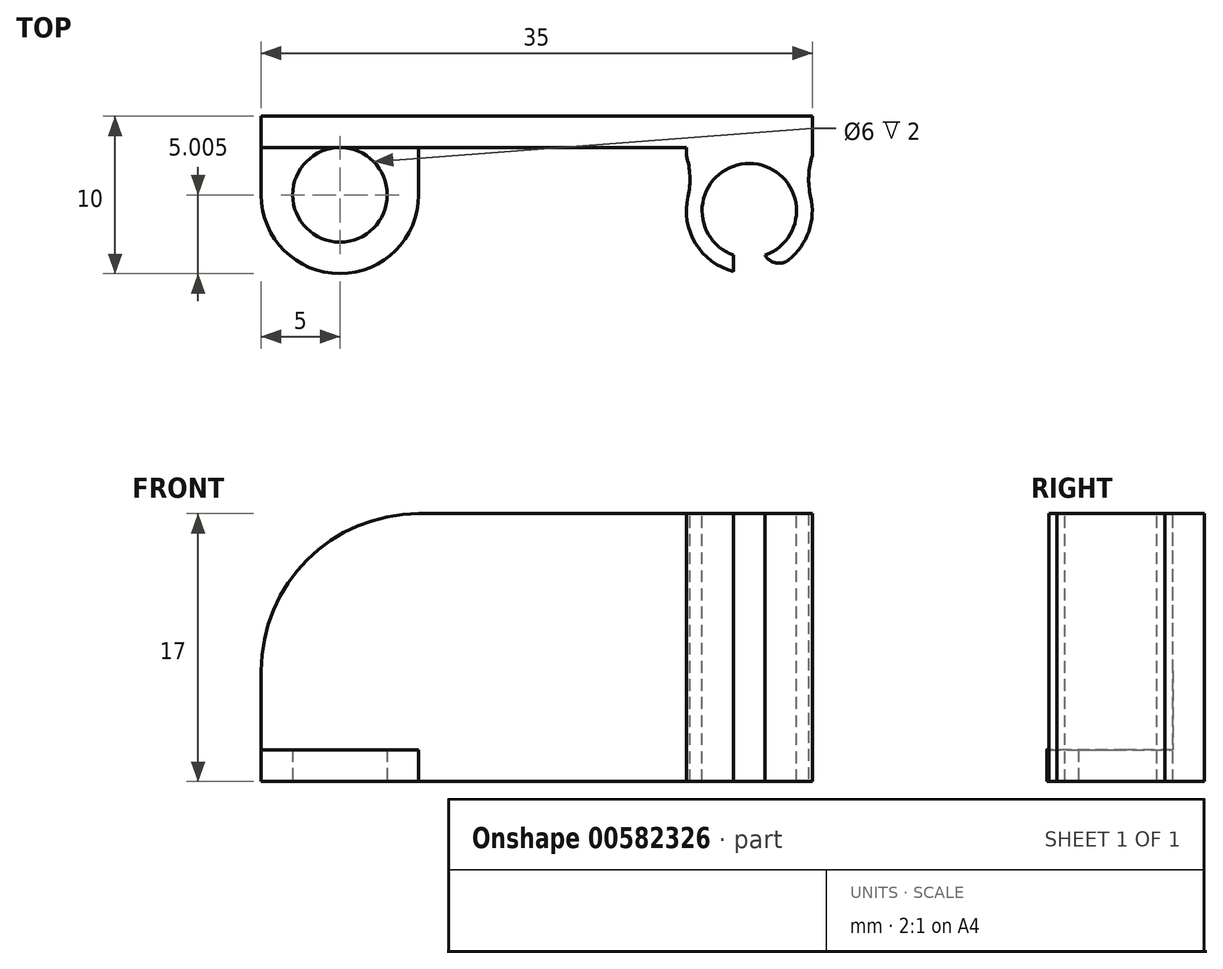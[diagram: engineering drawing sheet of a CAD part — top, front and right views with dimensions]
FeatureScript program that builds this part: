
annotation { "Feature Type Name" : "Feature", "Feature Type Description" : "" }
export const myFeature = defineFeature(function(context is Context, id is Id, definition is map)
    precondition{}
    {
        {
            var Q0;
            Q0=qCreatedBy(makeId("Top.planeOp"),FACE);
            var sketch = newSketch(context, id + "F0", { "sketchPlane" : qUnion([Q0])});
            skLineSegment(sketch, "E0.bottom", {"start": v(-13.22, 16.13) * mm, "end": v(-3.22, 16.13) * mm});
            skLineSegment(sketch, "E0.top", {"start": v(-13.22, 6.13) * mm, "end": v(-3.22, 6.13) * mm});
            skLineSegment(sketch, "E0.left", {"start": v(-13.22, 16.13) * mm, "end": v(-13.22, 6.13) * mm});
            skLineSegment(sketch, "E0.right", {"start": v(-3.22, 16.13) * mm, "end": v(-3.22, 6.13) * mm});
            skSolve(sketch);
        }
        {
            var Q0;
            Q0 = qSketchRegion(id + "F0", true);
            extrude(context, id + "F1", {"entities" : qUnion([Q0]), "depth" : 2 * mm, "offsetDistance" : 25 * mm});
        }
        {
            var Q0;
            Q0=makeQuery(id+"F1.opExtrude","CAP_FACE",FACE,{"disambiguationData":[OSD([sQuery(id+"F0.wireOp",EDGE,"E0.bottom"),sQuery(id+"F0.wireOp",EDGE,"E0.top"),sQuery(id+"F0.wireOp",EDGE,"E0.left"),sQuery(id+"F0.wireOp",EDGE,"E0.right")])],"isStart":false});
            var sketch = newSketch(context, id + "F2", { "sketchPlane" : qUnion([Q0])});
            skLineSegment(sketch, "E1.bottom", {"start": v(-13.22, 16.13) * mm, "end": v(-3.22, 16.13) * mm});
            skLineSegment(sketch, "E1.top", {"start": v(-13.22, 14.13) * mm, "end": v(-3.22, 14.13) * mm});
            skLineSegment(sketch, "E1.left", {"start": v(-13.22, 16.13) * mm, "end": v(-13.22, 14.13) * mm});
            skLineSegment(sketch, "E1.right", {"start": v(-3.22, 16.13) * mm, "end": v(-3.22, 14.13) * mm});
            skSolve(sketch);
        }
        {
            var Q0;
            Q0 = qSketchRegion(id + "F2", true);
            extrude(context, id + "F3", {"entities" : qUnion([Q0]), "operationType" : NewBodyOperationType.ADD, "depth" : 15 * mm, "offsetDistance" : 25 * mm});
        }
        {
            var Q0;
            Q0=makeQuery(id+"F3.boolean.opBoolean","MERGE",FACE,{"derivedFrom":[makeQuery(id+"F1.opExtrude","SWEPT_FACE",FACE,{"disambiguationData":[OSD([sQuery(id+"F0.wireOp",EDGE,"E0.right")])]}),makeQuery(id+"F3.opExtrude","SWEPT_FACE",FACE,{"disambiguationData":[OSD([sQuery(id+"F2.wireOp",EDGE,"E1.right")])]})]});
            var sketch = newSketch(context, id + "F4", { "sketchPlane" : qUnion([Q0])});
            skLineSegment(sketch, "E2.bottom", {"start": v(16.13, 0) * mm, "end": v(14.13, 0) * mm});
            skLineSegment(sketch, "E2.top", {"start": v(16.13, 17) * mm, "end": v(14.13, 17) * mm});
            skLineSegment(sketch, "E2.left", {"start": v(16.13, 0) * mm, "end": v(16.13, 17) * mm});
            skLineSegment(sketch, "E2.right", {"start": v(14.13, 0) * mm, "end": v(14.13, 17) * mm});
            skSolve(sketch);
        }
        {
            var Q0;
            Q0 = qSketchRegion(id + "F4", true);
            extrude(context, id + "F5", {"entities" : qUnion([Q0]), "operationType" : NewBodyOperationType.ADD, "depth" : 25 * mm, "offsetDistance" : 25 * mm});
        }
        {
            var Q0;
            Q0=makeQuery(id+"F5.boolean.opBoolean","MERGE",FACE,{"derivedFrom":[makeQuery(id+"F3.opExtrude","SWEPT_FACE",FACE,{"disambiguationData":[OSD([sQuery(id+"F2.wireOp",EDGE,"E1.top")])]}),makeQuery(id+"F5.opExtrude","SWEPT_FACE",FACE,{"disambiguationData":[OSD([sQuery(id+"F4.wireOp",EDGE,"E2.right")])]})]});
            var sketch = newSketch(context, id + "F6", { "sketchPlane" : qUnion([Q0])});
            skLineSegment(sketch, "E3.bottom", {"start": v(21.78, 17) * mm, "end": v(13.78, 17) * mm});
            skLineSegment(sketch, "E3.top", {"start": v(21.78, 16) * mm, "end": v(13.78, 16) * mm});
            skLineSegment(sketch, "E3.left", {"start": v(21.78, 17) * mm, "end": v(21.78, 16) * mm});
            skLineSegment(sketch, "E3.right", {"start": v(13.78, 17) * mm, "end": v(13.78, 16) * mm});
            skSolve(sketch);
        }
        {
            var Q0;
            Q0 = qSketchRegion(id + "F6", true);
            extrude(context, id + "F7", {"entities" : qUnion([Q0]), "operationType" : NewBodyOperationType.ADD, "depth" : 8 * mm, "offsetDistance" : 25 * mm});
        }
        {
            var Q0;
            Q0=makeQuery(id+"F7.opExtrude","SWEPT_FACE",FACE,{"disambiguationData":[OSD([sQuery(id+"F6.wireOp",EDGE,"E3.top")])]});
            var sketch = newSketch(context, id + "F8", { "sketchPlane" : qUnion([Q0])});
            skPoint(sketch, "E4", {"position": v(17.78, -10.13) * mm});
            skPoint(sketch, "E4.positionSnap0", {"position": v(17.78, -6.12) * mm});
            skPoint(sketch, "E4.positionSnap1", {"position": v(13.78, -10.13) * mm});
            skCircle(sketch, "E5", {"center": v(17.78, -10.13) * mm, "radius": 4 * mm});
            skCircle(sketch, "E6", {"center": v(17.78, -10.13) * mm, "radius": 3 * mm});
            skSolve(sketch);
        }
        {
            var Q0;
            Q0 = qSketchRegion(id + "F8", true);
            extrude(context, id + "F9", {"entities" : qUnion([Q0]), "operationType" : NewBodyOperationType.ADD, "depth" : 16 * mm, "offsetDistance" : 25 * mm});
        }
        {
            var Q0;
            Q0=makeQuery(id+"F9.boolean.opBoolean","SPLIT",FACE,{"disambiguationData":[TD([makeQuery(id+"F9.opExtrude","SWEPT_FACE",FACE,{"disambiguationData":[OSD([sQuery(id+"F8.wireOp",EDGE,"E6")])]})])],"derivedFrom":makeQuery(id+"F7.opExtrude","SWEPT_FACE",FACE,{"disambiguationData":[OSD([sQuery(id+"F6.wireOp",EDGE,"E3.top")])]})});
            var Q1;
            {var subQ1=makeQuery(id+"F7.opExtrude","SWEPT_FACE",FACE,{"disambiguationData":[OSD([sQuery(id+"F6.wireOp",EDGE,"E3.top")])]});Q1=makeQuery(id+"F9.boolean.opBoolean","SPLIT",FACE,{"disambiguationData":[TD([makeQuery(id+"F3.opExtrude","SWEPT_FACE",FACE,{"disambiguationData":[OSD([sQuery(id+"F2.wireOp",EDGE,"E1.top")])]})])],"derivedFrom":subQ1});}
            var Q2;
            {var subQ0=sQuery(id+"F6.wireOp",EDGE,"E3.left");var subQ1=sQuery(id+"F6.wireOp",EDGE,"E3.right");var subQ2=sQuery(id+"F6.wireOp",EDGE,"E3.top");var subQ3=makeQuery(id+"F7.opExtrude","SWEPT_FACE",FACE,{"disambiguationData":[OSD([subQ2])]});Q2=makeQuery(id+"F9.boolean.opBoolean","SPLIT",FACE,{"disambiguationData":[TD([makeQuery(id+"F7.opExtrude","CAP_FACE",FACE,{"disambiguationData":[OSD([sQuery(id+"F6.wireOp",EDGE,"E3.bottom"),subQ2,subQ0,subQ1])],"isStart":false})])],"derivedFrom":subQ3});}
            extrude(context, id + "F10", {"entities" : qUnion([Q0, Q1, Q2]), "operationType" : NewBodyOperationType.REMOVE, "oppositeDirection" : true, "depth" : 25 * mm, "offsetDistance" : 25 * mm});
        }
        {
            var Q0;
            {var subQ0=sQuery(id+"F6.wireOp",EDGE,"E3.top");Q0=makeQuery(id+"F10.boolean.opBoolean","MERGE",FACE,{"derivedFrom":[makeQuery(id+"F5.boolean.opBoolean","MERGE",FACE,{"derivedFrom":[makeQuery(id+"F3.opExtrude","SWEPT_FACE",FACE,{"disambiguationData":[OSD([sQuery(id+"F2.wireOp",EDGE,"E1.top")])]}),makeQuery(id+"F5.opExtrude","SWEPT_FACE",FACE,{"disambiguationData":[OSD([sQuery(id+"F4.wireOp",EDGE,"E2.right")])]})]}),makeQuery(id+"F10.opExtrude","SWEPT_FACE",FACE,{"disambiguationData":[OSD([subQ0]),TDD([makeQuery(id+"F7.opExtrude","CAP_EDGE",EDGE,{"disambiguationData":[OSD([subQ0])],"isStart":true})])]})]});}
            var sketch = newSketch(context, id + "F11", { "sketchPlane" : qUnion([Q0])});
            skLineSegment(sketch, "E7.bottom", {"start": v(21.78, 0) * mm, "end": v(13.78, 0) * mm});
            skLineSegment(sketch, "E7.top", {"start": v(21.78, 17) * mm, "end": v(13.78, 17) * mm});
            skLineSegment(sketch, "E7.left", {"start": v(21.78, 0) * mm, "end": v(21.78, 17) * mm});
            skLineSegment(sketch, "E7.right", {"start": v(13.78, 0) * mm, "end": v(13.78, 17) * mm});
            skSolve(sketch);
        }
        {
            var Q0;
            Q0 = qSketchRegion(id + "F11", true);
            extrude(context, id + "F12", {"entities" : qUnion([Q0]), "depth" : 0.5 * mm, "offsetDistance" : 25 * mm});
        }
        {
            var Q0;
            Q0=makeQuery(id+"F10.boolean.opBoolean","SPLIT",BODY,{"disambiguationData":[OD(0.0)],"derivedFrom":makeQuery(id+"F1.opExtrude","SWEPT_BODY",BODY,{"disambiguationData":[OSD([sQuery(id+"F0.wireOp",EDGE,"E0.bottom"),sQuery(id+"F0.wireOp",EDGE,"E0.top"),sQuery(id+"F0.wireOp",EDGE,"E0.left"),sQuery(id+"F0.wireOp",EDGE,"E0.right")])]})});
            var Q1;
            Q1=makeQuery(id+"F10.boolean.opBoolean","SPLIT",BODY,{"disambiguationData":[OD(1.0)],"derivedFrom":makeQuery(id+"F1.opExtrude","SWEPT_BODY",BODY,{"disambiguationData":[OSD([sQuery(id+"F0.wireOp",EDGE,"E0.bottom"),sQuery(id+"F0.wireOp",EDGE,"E0.top"),sQuery(id+"F0.wireOp",EDGE,"E0.left"),sQuery(id+"F0.wireOp",EDGE,"E0.right")])]})});
            var Q2;
            Q2=makeQuery(id+"F12.opExtrude","SWEPT_BODY",BODY,{"disambiguationData":[OSD([sQuery(id+"F11.wireOp",EDGE,"E7.bottom"),sQuery(id+"F11.wireOp",EDGE,"E7.top"),sQuery(id+"F11.wireOp",EDGE,"E7.left"),sQuery(id+"F11.wireOp",EDGE,"E7.right")])]});
            booleanBodies(context, id + "F13", {"operationType" : BooleanOperationType.UNION, "tools" : qUnion([Q0, Q1, Q2])});
        }
        {
            var Q0;
            {var subQ0=sQuery(id+"F8.wireOp",EDGE,"E5");var subQ1=makeQuery(id+"F9.opExtrude","CAP_EDGE",EDGE,{"disambiguationData":[OSD([subQ0])],"isStart":true});Q0=makeQuery(id+"F13.opBoolean","INTERSECT",EDGE,{"disambiguationData":[OD(1.0)],"derivedFrom":[makeQuery(id+"F10.boolean.opBoolean","MERGE",FACE,{"derivedFrom":[makeQuery(id+"F9.opExtrude","SWEPT_FACE",FACE,{"disambiguationData":[OSD([subQ0])]}),makeQuery(id+"F10.opExtrude","SWEPT_FACE",FACE,{"disambiguationData":[OSD([subQ0]),TDD([makeQuery(id+"F9.boolean.opBoolean","SPLIT",EDGE,{"disambiguationData":[OD(0.0)],"derivedFrom":subQ1})])]}),makeQuery(id+"F10.opExtrude","SWEPT_FACE",FACE,{"disambiguationData":[OSD([subQ0]),TDD([makeQuery(id+"F9.boolean.opBoolean","SPLIT",EDGE,{"disambiguationData":[OD(1.0)],"derivedFrom":subQ1})])]})]}),makeQuery(id+"F12.opExtrude","CAP_FACE",FACE,{"disambiguationData":[OSD([sQuery(id+"F11.wireOp",EDGE,"E7.bottom"),sQuery(id+"F11.wireOp",EDGE,"E7.top"),sQuery(id+"F11.wireOp",EDGE,"E7.left"),sQuery(id+"F11.wireOp",EDGE,"E7.right")])],"isStart":false})]});}
            var Q1;
            {var subQ0=sQuery(id+"F8.wireOp",EDGE,"E5");var subQ1=makeQuery(id+"F9.opExtrude","CAP_EDGE",EDGE,{"disambiguationData":[OSD([subQ0])],"isStart":true});Q1=makeQuery(id+"F13.opBoolean","INTERSECT",EDGE,{"disambiguationData":[OD(0.0)],"derivedFrom":[makeQuery(id+"F10.boolean.opBoolean","MERGE",FACE,{"derivedFrom":[makeQuery(id+"F9.opExtrude","SWEPT_FACE",FACE,{"disambiguationData":[OSD([subQ0])]}),makeQuery(id+"F10.opExtrude","SWEPT_FACE",FACE,{"disambiguationData":[OSD([subQ0]),TDD([makeQuery(id+"F9.boolean.opBoolean","SPLIT",EDGE,{"disambiguationData":[OD(0.0)],"derivedFrom":subQ1})])]}),makeQuery(id+"F10.opExtrude","SWEPT_FACE",FACE,{"disambiguationData":[OSD([subQ0]),TDD([makeQuery(id+"F9.boolean.opBoolean","SPLIT",EDGE,{"disambiguationData":[OD(1.0)],"derivedFrom":subQ1})])]})]}),makeQuery(id+"F12.opExtrude","CAP_FACE",FACE,{"disambiguationData":[OSD([sQuery(id+"F11.wireOp",EDGE,"E7.bottom"),sQuery(id+"F11.wireOp",EDGE,"E7.top"),sQuery(id+"F11.wireOp",EDGE,"E7.left"),sQuery(id+"F11.wireOp",EDGE,"E7.right")])],"isStart":false})]});}
            fillet(context, id + "F14", {"entities" : qUnion([Q0, Q1]), "radius" : 5 * mm, "tangentPropagation" : true, "allowEdgeOverflow" : false});
        }
        {
            var Q0;
            Q0=makeQuery(id+"F1.opExtrude","SWEPT_EDGE",EDGE,{"disambiguationData":[OSD([sQuery(id+"F0.wireOp",EDGE,"E0.top"),sQuery(id+"F0.wireOp",EDGE,"E0.left")])]});
            var Q1;
            Q1=makeQuery(id+"F1.opExtrude","SWEPT_EDGE",EDGE,{"disambiguationData":[OSD([sQuery(id+"F0.wireOp",EDGE,"E0.top"),sQuery(id+"F0.wireOp",EDGE,"E0.right")])]});
            fillet(context, id + "F15", {"entities" : qUnion([Q0, Q1]), "radius" : 5 * mm, "tangentPropagation" : true, "allowEdgeOverflow" : false});
        }
        {
            var Q0;
            Q0=makeQuery(id+"F13.opBoolean","MERGE",FACE,{"derivedFrom":[makeQuery(id+"F5.boolean.opBoolean","MERGE",FACE,{"derivedFrom":[makeQuery(id+"F1.opExtrude","CAP_FACE",FACE,{"disambiguationData":[OSD([sQuery(id+"F0.wireOp",EDGE,"E0.bottom"),sQuery(id+"F0.wireOp",EDGE,"E0.top"),sQuery(id+"F0.wireOp",EDGE,"E0.left"),sQuery(id+"F0.wireOp",EDGE,"E0.right")])],"isStart":true}),makeQuery(id+"F5.opExtrude","SWEPT_FACE",FACE,{"disambiguationData":[OSD([sQuery(id+"F4.wireOp",EDGE,"E2.bottom")])]})]}),makeQuery(id+"F9.opExtrude","CAP_FACE",FACE,{"disambiguationData":[OSD([sQuery(id+"F8.wireOp",EDGE,"E5"),sQuery(id+"F8.wireOp",EDGE,"E6")])],"isStart":false}),makeQuery(id+"F12.opExtrude","SWEPT_FACE",FACE,{"disambiguationData":[OSD([sQuery(id+"F11.wireOp",EDGE,"E7.bottom")])]})]});
            var sketch = newSketch(context, id + "F16", { "sketchPlane" : qUnion([Q0])});
            skPoint(sketch, "E8", {"position": v(-8.22, -11.13) * mm});
            skCircle(sketch, "E9", {"center": v(-8.22, -11.13) * mm, "radius": 3 * mm});
            skSolve(sketch);
        }
        {
            var Q0;
            Q0 = qSketchRegion(id + "F16", true);
            extrude(context, id + "F17", {"entities" : qUnion([Q0]), "operationType" : NewBodyOperationType.REMOVE, "oppositeDirection" : true, "depth" : 25 * mm, "offsetDistance" : 25 * mm});
        }
        {
            var Q0;
            Q0=makeQuery(id+"F3.opExtrude","CAP_EDGE",EDGE,{"disambiguationData":[OSD([sQuery(id+"F2.wireOp",EDGE,"E1.left")])],"isStart":false});
            fillet(context, id + "F18", {"entities" : qUnion([Q0]), "radius" : 10 * mm, "tangentPropagation" : true, "allowEdgeOverflow" : false});
        }
        {
            var Q0;
            {var subQ0=sQuery(id+"F8.wireOp",EDGE,"E5");var subQ3=sQuery(id+"F4.wireOp",EDGE,"E2.top");var subQ4=sQuery(id+"F2.wireOp",EDGE,"E1.left");var subQ5=sQuery(id+"F2.wireOp",EDGE,"E1.top");var subQ6=sQuery(id+"F2.wireOp",EDGE,"E1.bottom");var subQ7=makeQuery(id+"F7.boolean.opBoolean","MERGE",FACE,{"derivedFrom":[makeQuery(id+"F5.boolean.opBoolean","MERGE",FACE,{"derivedFrom":[makeQuery(id+"F3.opExtrude","CAP_FACE",FACE,{"disambiguationData":[OSD([subQ6,subQ5,subQ4,sQuery(id+"F2.wireOp",EDGE,"E1.right")])],"isStart":false}),makeQuery(id+"F5.opExtrude","SWEPT_FACE",FACE,{"disambiguationData":[OSD([subQ3])]})]}),makeQuery(id+"F7.opExtrude","SWEPT_FACE",FACE,{"disambiguationData":[OSD([sQuery(id+"F6.wireOp",EDGE,"E3.bottom")])]})]});Q0=makeQuery(id+"F13.opBoolean","MERGE",FACE,{"derivedFrom":[makeQuery(id+"F10.boolean.opBoolean","SPLIT",FACE,{"disambiguationData":[TD([makeQuery(id+"F1.opExtrude","SWEPT_FACE",FACE,{"disambiguationData":[OSD([sQuery(id+"F0.wireOp",EDGE,"E0.bottom")])]})])],"derivedFrom":subQ7}),makeQuery(id+"F10.boolean.opBoolean","SPLIT",FACE,{"disambiguationData":[TD([makeQuery(id+"F9.opExtrude","SWEPT_FACE",FACE,{"disambiguationData":[OSD([subQ0])]})])],"derivedFrom":subQ7}),makeQuery(id+"F12.opExtrude","SWEPT_FACE",FACE,{"disambiguationData":[OSD([sQuery(id+"F11.wireOp",EDGE,"E7.top")])]})]});}
            var sketch = newSketch(context, id + "F19", { "sketchPlane" : qUnion([Q0])});
            skLineSegment(sketch, "E10", {"start": v(17.78, 6.13) * mm, "end": v(17.78, 7.13) * mm});
            skLineSegment(sketch, "E11", {"start": v(16.78, 7.3) * mm, "end": v(16.78, 6.26) * mm});
            skLineSegment(sketch, "E12", {"start": v(18.78, 6.26) * mm, "end": v(18.78, 7.3) * mm});
            skSolve(sketch);
        }
        {
            var Q0;
            {var subQ0=sQuery(id+"F19.wireOp",EDGE,"E10");Q0=makeQuery(id+"F19.imprint","IMPRINT",FACE,{"disambiguationData":[TD([[makeQuery(id+"F19.imprint","IMPRINT",EDGE,{"derivedFrom":subQ0}),1.0]])]});}
            var Q1;
            {var subQ0=sQuery(id+"F19.wireOp",EDGE,"E10");Q1=makeQuery(id+"F19.imprint","IMPRINT",FACE,{"disambiguationData":[TD([[makeQuery(id+"F19.imprint","IMPRINT",EDGE,{"derivedFrom":subQ0}),-1.0]])]});}
            extrude(context, id + "F20", {"entities" : qUnion([Q0, Q1]), "operationType" : NewBodyOperationType.REMOVE, "oppositeDirection" : true, "depth" : 25 * mm, "offsetDistance" : 25 * mm});
        }
        {
            var Q0;
            Q0=makeQuery(id+"F20.boolean.opBoolean","COPY",EDGE,{"derivedFrom":makeQuery(id+"F20.opExtrude","SWEPT_EDGE",EDGE,{"disambiguationData":[OSD([sQuery(id+"F2.wireOp",EDGE,"E1.bottom"),sQuery(id+"F2.wireOp",EDGE,"E1.top"),sQuery(id+"F2.wireOp",EDGE,"E1.left"),sQuery(id+"F2.wireOp",EDGE,"E1.right"),sQuery(id+"F4.wireOp",EDGE,"E2.top"),sQuery(id+"F6.wireOp",EDGE,"E3.bottom"),sQuery(id+"F8.wireOp",EDGE,"E5"),sQuery(id+"F19.wireOp",EDGE,"E12")])]})});
            var Q1;
            Q1=makeQuery(id+"F20.boolean.opBoolean","COPY",EDGE,{"derivedFrom":makeQuery(id+"F20.opExtrude","SWEPT_EDGE",EDGE,{"disambiguationData":[OSD([sQuery(id+"F2.wireOp",EDGE,"E1.bottom"),sQuery(id+"F2.wireOp",EDGE,"E1.top"),sQuery(id+"F2.wireOp",EDGE,"E1.left"),sQuery(id+"F2.wireOp",EDGE,"E1.right"),sQuery(id+"F4.wireOp",EDGE,"E2.top"),sQuery(id+"F6.wireOp",EDGE,"E3.bottom"),sQuery(id+"F8.wireOp",EDGE,"E5"),sQuery(id+"F19.wireOp",EDGE,"E11")])]})});
            fillet(context, id + "F21", {"entities" : qUnion([Q0, Q1]), "radius" : 1 * mm, "tangentPropagation" : true, "allowEdgeOverflow" : false});
        }
    });
